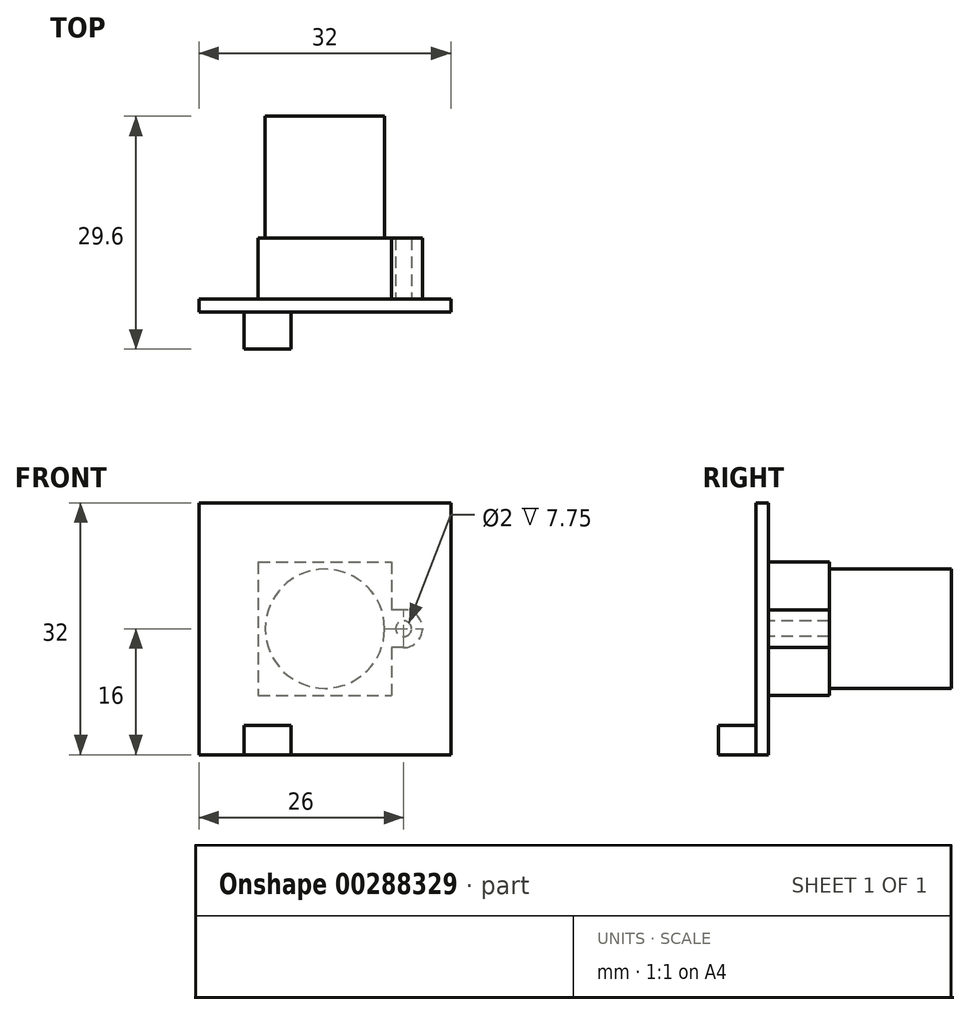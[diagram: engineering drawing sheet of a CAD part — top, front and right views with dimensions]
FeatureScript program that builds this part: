
annotation { "Feature Type Name" : "Feature", "Feature Type Description" : "" }
export const myFeature = defineFeature(function(context is Context, id is Id, definition is map)
    precondition{}
    {
        {
            var Q0;
            Q0=qCreatedBy(makeId("Front.planeOp"),FACE);
            var sketch = newSketch(context, id + "F0", { "sketchPlane" : qUnion([Q0])});
            skLineSegment(sketch, "E0.bottom", {"start": v(16, -16) * mm, "end": v(-16, -16) * mm});
            skLineSegment(sketch, "E0.top", {"start": v(16, 16) * mm, "end": v(-16, 16) * mm});
            skLineSegment(sketch, "E0.left", {"start": v(16, -16) * mm, "end": v(16, 16) * mm});
            skLineSegment(sketch, "E0.right", {"start": v(-16, -16) * mm, "end": v(-16, 16) * mm});
            skPoint(sketch, "E0.middle", {"position": v(0, 0) * mm});
            skSolve(sketch);
        }
        {
            var Q0;
            Q0 = qSketchRegion(id + "F0", true);
            extrude(context, id + "F1", {"entities" : qUnion([Q0]), "depth" : 1.6 * mm});
        }
        {
            var Q0;
            Q0=makeQuery(id+"F1.opExtrude","CAP_FACE",FACE,{"disambiguationData":[OSD([sQuery(id+"F0.wireOp",EDGE,"E0.bottom"),sQuery(id+"F0.wireOp",EDGE,"E0.top"),sQuery(id+"F0.wireOp",EDGE,"E0.left"),sQuery(id+"F0.wireOp",EDGE,"E0.right")])],"isStart":false});
            var sketch = newSketch(context, id + "F2", { "sketchPlane" : qUnion([Q0])});
            skLineSegment(sketch, "E1.bottom", {"start": v(-10.25, -16) * mm, "end": v(-4.3, -16) * mm});
            skLineSegment(sketch, "E1.top", {"start": v(-10.25, -12.3) * mm, "end": v(-4.3, -12.3) * mm});
            skLineSegment(sketch, "E1.left", {"start": v(-10.25, -16) * mm, "end": v(-10.25, -12.3) * mm});
            skLineSegment(sketch, "E1.right", {"start": v(-4.3, -16) * mm, "end": v(-4.3, -12.3) * mm});
            skSolve(sketch);
        }
        {
            var Q0;
            Q0 = qSketchRegion(id + "F2", true);
            extrude(context, id + "F3", {"entities" : qUnion([Q0]), "operationType" : NewBodyOperationType.ADD, "depth" : 4.75 * mm});
        }
        {
            var Q0;
            Q0=makeQuery(id+"F1.opExtrude","CAP_FACE",FACE,{"disambiguationData":[OSD([sQuery(id+"F0.wireOp",EDGE,"E0.bottom"),sQuery(id+"F0.wireOp",EDGE,"E0.top"),sQuery(id+"F0.wireOp",EDGE,"E0.left"),sQuery(id+"F0.wireOp",EDGE,"E0.right")])],"isStart":true});
            var sketch = newSketch(context, id + "F4", { "sketchPlane" : qUnion([Q0])});
            skLineSegment(sketch, "E2.bottom", {"start": v(8.47, 8.47) * mm, "end": v(-8.47, 8.47) * mm});
            skLineSegment(sketch, "E2.top", {"start": v(8.47, -8.47) * mm, "end": v(-8.48, -8.47) * mm});
            skLineSegment(sketch, "E2.left", {"start": v(8.47, 8.47) * mm, "end": v(8.47, -8.47) * mm});
            skLineSegment(sketch, "E2.right", {"start": v(-8.47, 8.47) * mm, "end": v(-8.48, -8.47) * mm});
            skPoint(sketch, "E2.middle", {"position": v(0, 0) * mm});
            skSolve(sketch);
        }
        {
            var Q0;
            Q0 = qSketchRegion(id + "F4", true);
            extrude(context, id + "F5", {"entities" : qUnion([Q0]), "operationType" : NewBodyOperationType.ADD, "depth" : 7.75 * mm});
        }
        {
            var Q0;
            Q0=makeQuery(id+"F5.opExtrude","CAP_FACE",FACE,{"disambiguationData":[OSD([sQuery(id+"F4.wireOp",EDGE,"E2.bottom"),sQuery(id+"F4.wireOp",EDGE,"E2.top"),sQuery(id+"F4.wireOp",EDGE,"E2.left"),sQuery(id+"F4.wireOp",EDGE,"E2.right")])],"isStart":false});
            var sketch = newSketch(context, id + "F6", { "sketchPlane" : qUnion([Q0])});
            skCircle(sketch, "E3", {"center": v(0, 0) * mm, "radius": 7.58 * mm});
            skSolve(sketch);
        }
        {
            var Q0;
            Q0 = qSketchRegion(id + "F6", true);
            extrude(context, id + "F7", {"entities" : qUnion([Q0]), "operationType" : NewBodyOperationType.ADD, "depth" : 15.5 * mm});
        }
        {
            var Q0;
            Q0=makeQuery(id+"F1.opExtrude","CAP_FACE",FACE,{"disambiguationData":[OSD([sQuery(id+"F0.wireOp",EDGE,"E0.bottom"),sQuery(id+"F0.wireOp",EDGE,"E0.top"),sQuery(id+"F0.wireOp",EDGE,"E0.left"),sQuery(id+"F0.wireOp",EDGE,"E0.right")])],"isStart":true});
            var sketch = newSketch(context, id + "F8", { "sketchPlane" : qUnion([Q0])});
            skLineSegment(sketch, "E4", {"start": v(0, 0) * mm, "end": v(-10, 0) * mm, "construction": true});
            skPoint(sketch, "E4.endSnap0", {"position": v(-8.48, 0) * mm});
            skCircle(sketch, "E5", {"center": v(-10, 0) * mm, "radius": 1 * mm});
            skArc(sketch, "E6", {"start": v(-10, 2.4) * mm, "mid": v(-12.4, 0) * mm, "end": v(-10, -2.4) * mm});
            skLineSegment(sketch, "E7", {"start": v(-10, 0) * mm, "end": v(-10, 2.4) * mm, "construction": true});
            skLineSegment(sketch, "E8", {"start": v(-10, 0) * mm, "end": v(-10, -2.4) * mm, "construction": true});
            skLineSegment(sketch, "E9", {"start": v(-10, 2.4) * mm, "end": v(-8.48, 2.4) * mm});
            skLineSegment(sketch, "E10", {"start": v(-8.48, 2.4) * mm, "end": v(-8.48, -2.4) * mm});
            skLineSegment(sketch, "E11", {"start": v(-10, -2.4) * mm, "end": v(-8.48, -2.4) * mm});
            skSolve(sketch);
        }
        {
            var Q0;
            Q0 = qSketchRegion(id + "F8", true);
            extrude(context, id + "F9", {"entities" : qUnion([Q0]), "operationType" : NewBodyOperationType.ADD, "depth" : 7.75 * mm});
        }
    });
